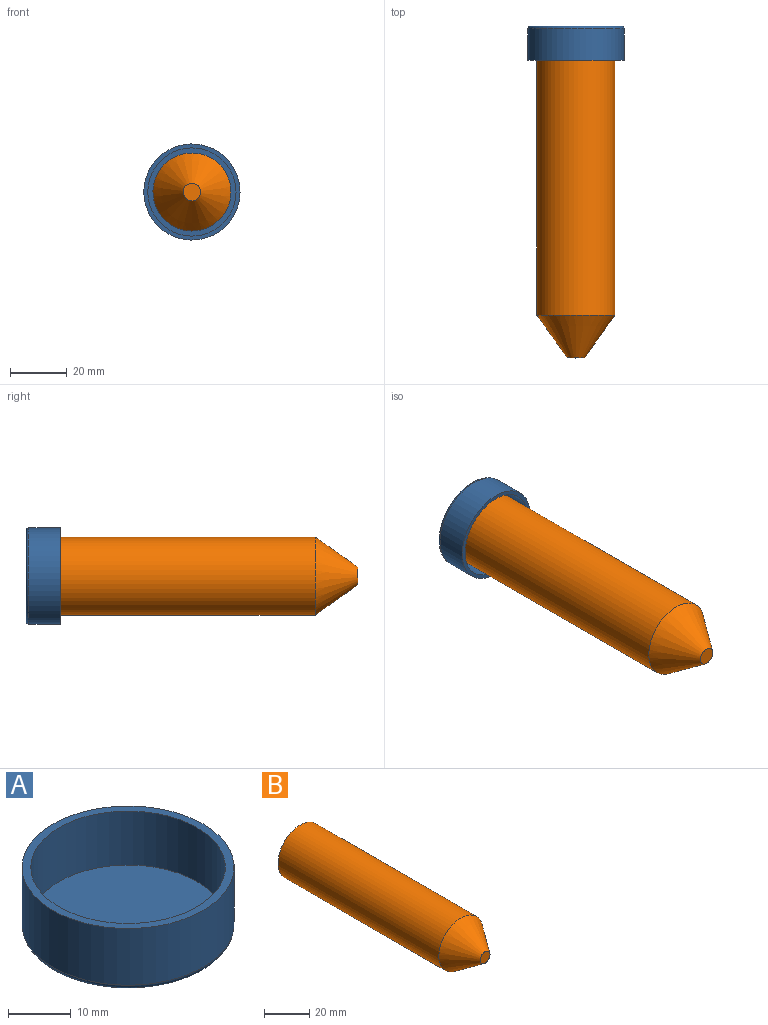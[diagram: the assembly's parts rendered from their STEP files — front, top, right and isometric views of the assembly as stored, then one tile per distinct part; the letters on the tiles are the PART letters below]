
ASSEMBLY  parts=2 mates=1
PART A: 6 faces, bbox 36.7x36.7x12.1 mm
  f0: cylinder r=16.95mm len=33.9mm, axis (0,0,-1), area 1182.1mm2, adj f1,f5
  f1: plane 33.9x33.9mm, normal (0,0,1), area 142.9mm2, adj f0,f3
  f2: plane 31.9x31.9mm, normal (0,0,-1), area 799.2mm2, adj f5
  f3: cylinder r=15.55mm len=31.1mm, axis (0,0,1), area 1030.8mm2, adj f1,f4
  f4: plane 31.1x31.1mm, normal (0,0,1), area 759.6mm2, adj f3
  f5: torus R=15.95mm, axis (0,0,1), area 163.7mm2, adj f0,f2
PART B: 7 faces, bbox 27.5x115.5x27.5 mm
  f0: plane 5.12x5.12mm, normal (0,1,0), area 20.6mm2, adj f6
  f1: plane 6.15x6.15mm, normal (0,-1,0), area 29.7mm2, adj f2
  f2: cone r=3.08mm half-angle=35.3deg, axis (0,1,0), area 978.6mm2, adj f1,f3
  f3: cylinder r=13.76mm len=100.4mm, axis (0,-1,0), area 8682.3mm2, adj f2,f4
  f4: plane 27.53x27.53mm, normal (0,1,0), area 83.3mm2, adj f3,f5
  f5: cylinder r=12.76mm len=100.08mm, axis (0,-1,0), area 8026mm2, adj f4,f6
  f6: cone r=2.56mm half-angle=35.3deg, axis (0,1,0), area 850.2mm2, adj f0,f5
PLACE A rot(axis=(1,0,0),90deg) t=(0,117.05,0)mm
PLACE B at identity
MATE fastened A.f0 <-> B.f2  axis (0,-1,0) through (0,115.5,0)mm
